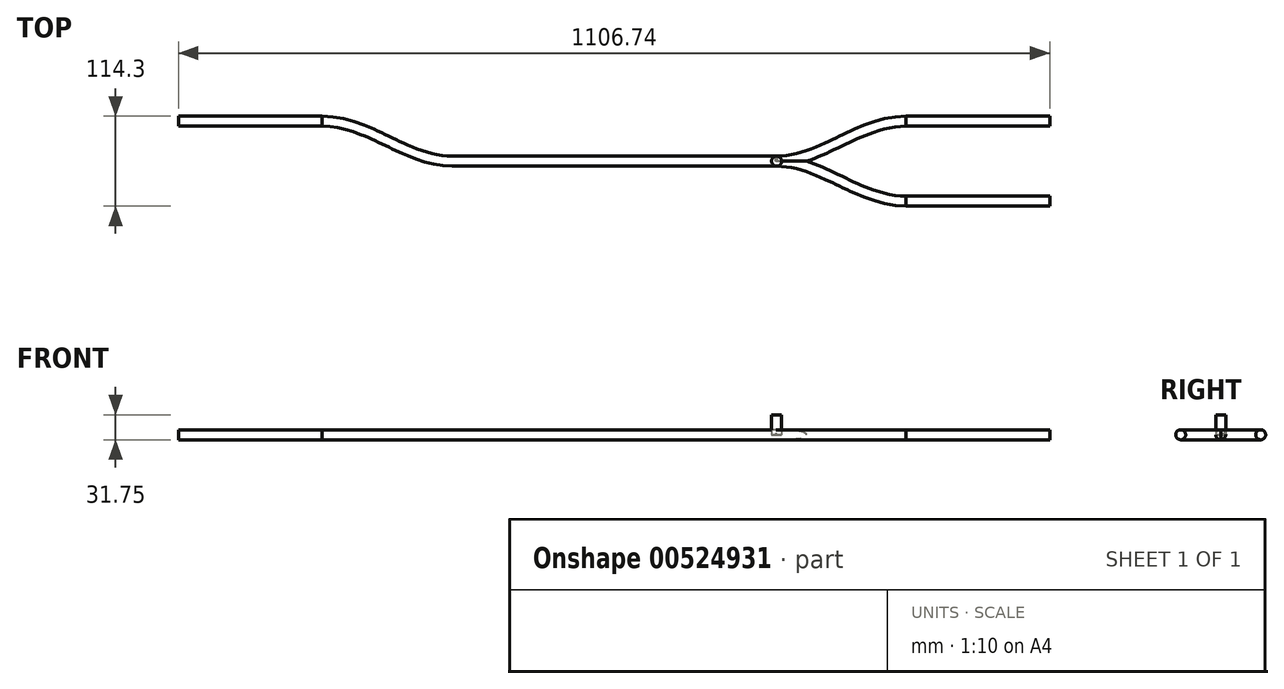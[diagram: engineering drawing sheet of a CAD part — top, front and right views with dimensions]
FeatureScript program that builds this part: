
annotation { "Feature Type Name" : "Feature", "Feature Type Description" : "" }
export const myFeature = defineFeature(function(context is Context, id is Id, definition is map)
    precondition{}
    {
        {
            var Q0;
            Q0=qCreatedBy(makeId("Right.planeOp"),FACE);
            var sketch = newSketch(context, id + "F0", { "sketchPlane" : qUnion([Q0])});
            skCircle(sketch, "E0", {"center": v(0, 0) * mm, "radius": 6.35 * mm});
            skSolve(sketch);
        }
        {
            var Q0;
            Q0=qCreatedBy(makeId("Top.planeOp"),FACE);
            var sketch = newSketch(context, id + "F1", { "sketchPlane" : qUnion([Q0])});
            skLineSegment(sketch, "E1", {"start": v(0, 0) * mm, "end": v(205.87, 0) * mm});
            skFitSpline(sketch, "E2", {"points": [v(205.87, 0) * mm, v(370.77, 50.8) * mm], "startDerivative": vector(174.15, 0) * mm, "endDerivative": vector(185.02, 2.24) * mm});
            skLineSegment(sketch, "E3", {"start": v(370.77, 50.8) * mm, "end": v(553.37, 50.8) * mm});
            skSolve(sketch);
        }
        {
            var Q0;
            Q0 = qSketchRegion(id + "F0", true);
            var Q1;
            Q1=sQuery(id+"F1.wireOp",EDGE,"E1");
            var Q2;
            Q2=sQuery(id+"F1.wireOp",EDGE,"E2");
            var Q3;
            Q3=sQuery(id+"F1.wireOp",EDGE,"E3");
            sweep(context, id + "F2", {"profiles" : qUnion([Q0]), "path" : qUnion([Q1, Q2, Q3])});
        }
        {
            var Q0;
            Q0=makeQuery(id+"F2.opSweep","SWEPT_BODY",BODY,{"disambiguationData":[OSD([sQuery(id+"F0.wireOp",EDGE,"E0"),sQuery(id+"F1.wireOp",EDGE,"E3")])]});
            var Q1;
            Q1=qCreatedBy(makeId("Right.planeOp"),FACE);
            mirror(context, id + "F3", {"entities" : qUnion([Q0]), "mirrorPlane" : qUnion([Q1])});
        }
        {
            var Q0;
            Q0=makeQuery(id+"F2.opSweep","SWEPT_BODY",BODY,{"disambiguationData":[OSD([sQuery(id+"F0.wireOp",EDGE,"E0"),sQuery(id+"F1.wireOp",EDGE,"E3")])]});
            var Q1;
            Q1=qCreatedBy(makeId("Front.planeOp"),FACE);
            mirror(context, id + "F4", {"operationType" : NewBodyOperationType.ADD, "entities" : qUnion([Q0]), "mirrorPlane" : qUnion([Q1])});
        }
        {
            var Q0;
            Q0=qCreatedBy(makeId("Top.planeOp"),FACE);
            var sketch = newSketch(context, id + "F5", { "sketchPlane" : qUnion([Q0])});
            skCircle(sketch, "E4", {"center": v(206.4, 0) * mm, "radius": 6.35 * mm});
            skSolve(sketch);
        }
        {
            var Q0;
            Q0 = qSketchRegion(id + "F5", true);
            var Q1;
            Q1=sQuery(id+"F5.wireOp",EDGE,"E4");
            extrude(context, id + "F6", {"entities" : qUnion([Q0]), "surfaceEntities" : qUnion([Q1]), "depth" : 25.4 * mm, "offsetDistance" : 25.4 * mm});
        }
        {
            var Q0;
            Q0=qCreatedBy(makeId("Front.planeOp"),FACE);
            var sketch = newSketch(context, id + "F7", { "sketchPlane" : qUnion([Q0])});
            skLineSegment(sketch, "E5", {"start": v(205.88, 0) * mm, "end": v(206.96, 30.23) * mm});
            skSolve(sketch);
        }
        {
            var Q0;
            Q0=sQuery(id+"F7.wireOp",VERTEX,"E5.start");
            var Q1;
            Q1=makeQuery(id+"F2.opSweep","SWEPT_BODY",BODY,{"disambiguationData":[OSD([sQuery(id+"F0.wireOp",EDGE,"E0"),sQuery(id+"F1.wireOp",EDGE,"E3")])]});
            var Q2;
            Q2=makeQuery(id+"F6.opExtrude","SWEPT_BODY",BODY,{"disambiguationData":[OSD([sQuery(id+"F5.wireOp",EDGE,"E4")])]});
            hole(context, id + "F8", {"style" : HoleStyle.SIMPLE, "endStyle" : HoleEndStyle.THROUGH, "holeDiameter" : 2.54 * mm, "isTappedThrough" : true, "tappedDepth" : 12.7 * mm, "tapClearance" : 3, "startFromSketch" : true, "locations" : qUnion([Q0]), "scope" : qUnion([Q1, Q2])});
        }
    });
